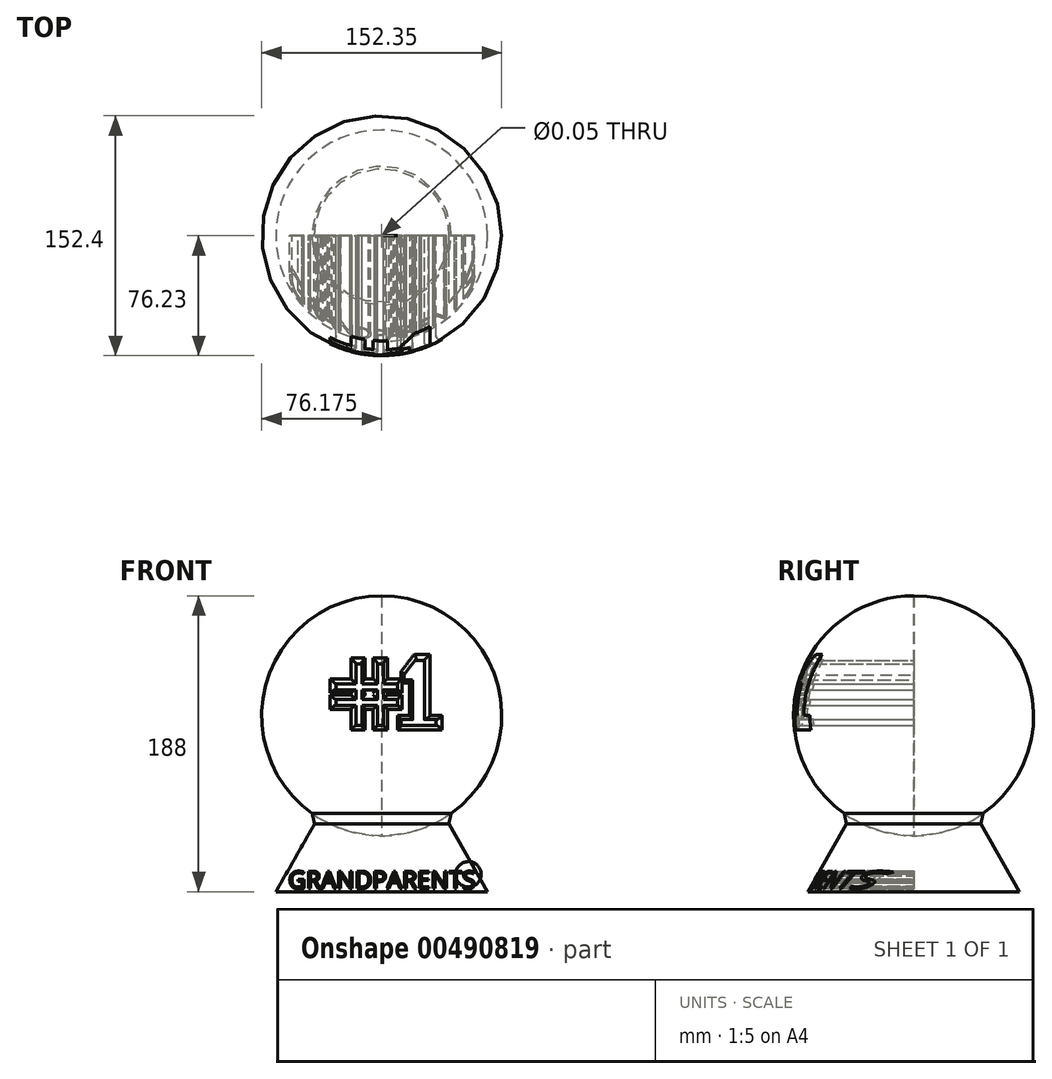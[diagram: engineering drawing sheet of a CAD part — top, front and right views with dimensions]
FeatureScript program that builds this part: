
annotation { "Feature Type Name" : "Feature", "Feature Type Description" : "" }
export const myFeature = defineFeature(function(context is Context, id is Id, definition is map)
    precondition{}
    {
        {
            var Q0;
            Q0=qCreatedBy(makeId("Front.planeOp"),FACE);
            var sketch = newSketch(context, id + "F0", { "sketchPlane" : qUnion([Q0])});
            skArc(sketch, "E0", {"start": v(0, 188) * mm, "mid": v(-76.2, 111.8) * mm, "end": v(0, 35.6) * mm});
            skLineSegment(sketch, "E1", {"start": v(0, 188) * mm, "end": v(0, 35.6) * mm});
            skLineSegment(sketch, "E2", {"start": v(0.03, 35.7) * mm, "end": v(0.03, 188.05) * mm, "construction": true});
            skSolve(sketch);
        }
        {
            var Q0;
            Q0 = qSketchRegion(id + "F0", true);
            var Q1;
            Q1=sQuery(id+"F0.wireOp",EDGE,"E2");
            revolve(context, id + "F1", {"entities" : qUnion([Q0]), "axis" : qUnion([Q1]), "revolveType" : RevolveType.FULL});
        }
        {
            var Q0;
            Q0=qCreatedBy(makeId("Front.planeOp"),FACE);
            var sketch = newSketch(context, id + "F2", { "sketchPlane" : qUnion([Q0])});
            skLineSegment(sketch, "E3", {"start": v(-40.05, 47.52) * mm, "end": v(-67.16, 0) * mm});
            skLineSegment(sketch, "E4", {"start": v(0, 0) * mm, "end": v(0, 64.85) * mm, "construction": true});
            skCircle(sketch, "E5", {"center": v(0, 112.35) * mm, "radius": 76.2 * mm, "construction": true});
            skArc(sketch, "E6", {"start": v(-40.05, 47.52) * mm, "mid": v(-20.9, 38.78) * mm, "end": v(0, 36.15) * mm});
            skLineSegment(sketch, "E7", {"start": v(-67.16, 0) * mm, "end": v(0, 0) * mm});
            skLineSegment(sketch, "E8", {"start": v(0, 0) * mm, "end": v(0, 36.15) * mm});
            skSolve(sketch);
        }
        {
            var Q0;
            Q0=makeQuery(id+"F2.imprint","IMPRINT",FACE,{"disambiguationData":[TD([[makeQuery(id+"F2.imprint","IMPRINT",EDGE,{"derivedFrom":sQuery(id+"F2.wireOp",EDGE,"E3")}),1.0]])]});
            var Q1;
            Q1=sQuery(id+"F2.wireOp",EDGE,"E4");
            revolve(context, id + "F3", {"operationType" : NewBodyOperationType.ADD, "entities" : qUnion([Q0]), "axis" : qUnion([Q1]), "revolveType" : RevolveType.FULL});
        }
        {
            var Q0;
            Q0=makeQuery(id+"F3.boolean.opBoolean","INTERSECT",EDGE,{"derivedFrom":[makeQuery(id+"F1.opRevolve","SWEPT_FACE",FACE,{"disambiguationData":[OSD([sQuery(id+"F0.wireOp",EDGE,"E0")])]}),makeQuery(id+"F3.opRevolve","SWEPT_FACE",FACE,{"disambiguationData":[OSD([sQuery(id+"F2.wireOp",EDGE,"E3")])]})]});
            chamfer(context, id + "F4", {"entities" : qUnion([Q0]), "width" : 5.08 * mm, "tangentPropagation" : true});
        }
        {
            var Q0;
            Q0=qCreatedBy(makeId("Front.planeOp"),FACE);
            var sketch = newSketch(context, id + "F5", { "sketchPlane" : qUnion([Q0])});
            skLineSegment(sketch, "E9", {"start": v(-16.4, 105.63) * mm, "end": v(-16.4, 128.2) * mm});
            skLineSegment(sketch, "E10", {"start": v(-2.72, 105.63) * mm, "end": v(-2.72, 128.2) * mm});
            skLineSegment(sketch, "E11", {"start": v(-29.1, 132) * mm, "end": v(9.98, 132) * mm});
            skLineSegment(sketch, "E12", {"start": v(-29.1, 118.33) * mm, "end": v(9.98, 118.33) * mm});
            skLineSegment(sketch, "E13", {"start": v(-29.1, 132) * mm, "end": v(-29.1, 128.2) * mm});
            skLineSegment(sketch, "E14", {"start": v(-29.1, 128.2) * mm, "end": v(9.98, 128.2) * mm});
            skLineSegment(sketch, "E15", {"start": v(9.98, 128.2) * mm, "end": v(9.98, 132) * mm});
            skLineSegment(sketch, "E16.trimOffspring", {"start": v(-16.4, 132) * mm, "end": v(-16.4, 144.7) * mm});
            skLineSegment(sketch, "E17.trimOffspring", {"start": v(-2.72, 132) * mm, "end": v(-2.72, 144.7) * mm});
            skLineSegment(sketch, "E18", {"start": v(-29.1, 118.33) * mm, "end": v(-29.1, 122.14) * mm});
            skLineSegment(sketch, "E19", {"start": v(-29.1, 122.14) * mm, "end": v(9.98, 122.14) * mm});
            skLineSegment(sketch, "E20", {"start": v(9.98, 118.33) * mm, "end": v(9.98, 122.14) * mm});
            skLineSegment(sketch, "E21", {"start": v(-16.4, 105.63) * mm, "end": v(-12.58, 105.63) * mm});
            skLineSegment(sketch, "E22", {"start": v(-12.58, 105.63) * mm, "end": v(-12.58, 144.7) * mm});
            skLineSegment(sketch, "E23", {"start": v(-16.4, 144.7) * mm, "end": v(-12.58, 144.7) * mm});
            skLineSegment(sketch, "E24", {"start": v(-2.72, 105.63) * mm, "end": v(1.1, 105.63) * mm});
            skLineSegment(sketch, "E25", {"start": v(1.1, 105.63) * mm, "end": v(1.1, 144.7) * mm});
            skLineSegment(sketch, "E26", {"start": v(1.1, 144.7) * mm, "end": v(-2.72, 144.7) * mm});
            skLineSegment(sketch, "E27", {"start": v(12.35, 105.7) * mm, "end": v(34.53, 105.7) * mm});
            skLineSegment(sketch, "E28", {"start": v(34.53, 105.7) * mm, "end": v(34.53, 109.31) * mm});
            skLineSegment(sketch, "E29", {"start": v(34.53, 109.31) * mm, "end": v(27.13, 109.31) * mm});
            skLineSegment(sketch, "E30", {"start": v(27.13, 109.31) * mm, "end": v(27.13, 147.04) * mm});
            skLineSegment(sketch, "E31", {"start": v(27.13, 147.04) * mm, "end": v(21.36, 147.04) * mm});
            skLineSegment(sketch, "E32", {"start": v(21.36, 147.04) * mm, "end": v(14.32, 137.86) * mm});
            skLineSegment(sketch, "E33", {"start": v(14.32, 137.86) * mm, "end": v(14.32, 134.55) * mm});
            skLineSegment(sketch, "E34", {"start": v(14.32, 134.55) * mm, "end": v(19.75, 134.55) * mm});
            skLineSegment(sketch, "E35", {"start": v(12.35, 105.7) * mm, "end": v(12.35, 109.31) * mm});
            skLineSegment(sketch, "E36", {"start": v(12.35, 109.31) * mm, "end": v(19.75, 109.31) * mm});
            skLineSegment(sketch, "E37", {"start": v(19.75, 109.31) * mm, "end": v(19.75, 134.55) * mm});
            skSolve(sketch);
        }
        {
            var Q0;
            Q0 = qSketchRegion(id + "F5", true);
            extrude(context, id + "F6", {"entities" : qUnion([Q0]), "operationType" : NewBodyOperationType.REMOVE, "depth" : 78.74 * mm});
        }
        {
            var Q0;
            Q0=makeQuery(id+"F6.boolean.opBoolean","INTERSECT",EDGE,{"derivedFrom":[makeQuery(id+"F1.opRevolve","SWEPT_FACE",FACE,{"disambiguationData":[OSD([sQuery(id+"F0.wireOp",EDGE,"E0")])]}),makeQuery(id+"F6.opExtrude","SWEPT_FACE",FACE,{"disambiguationData":[OSD([sQuery(id+"F5.wireOp",EDGE,"E30")])]})]});
            var Q1;
            Q1=makeQuery(id+"F6.boolean.opBoolean","INTERSECT",EDGE,{"derivedFrom":[makeQuery(id+"F1.opRevolve","SWEPT_FACE",FACE,{"disambiguationData":[OSD([sQuery(id+"F0.wireOp",EDGE,"E0")])]}),makeQuery(id+"F6.opExtrude","SWEPT_FACE",FACE,{"disambiguationData":[OSD([sQuery(id+"F5.wireOp",EDGE,"E29")])]})]});
            var Q2;
            Q2=makeQuery(id+"F6.boolean.opBoolean","INTERSECT",EDGE,{"derivedFrom":[makeQuery(id+"F1.opRevolve","SWEPT_FACE",FACE,{"disambiguationData":[OSD([sQuery(id+"F0.wireOp",EDGE,"E0")])]}),makeQuery(id+"F6.opExtrude","SWEPT_FACE",FACE,{"disambiguationData":[OSD([sQuery(id+"F5.wireOp",EDGE,"E28")])]})]});
            var Q3;
            Q3=makeQuery(id+"F6.boolean.opBoolean","INTERSECT",EDGE,{"derivedFrom":[makeQuery(id+"F1.opRevolve","SWEPT_FACE",FACE,{"disambiguationData":[OSD([sQuery(id+"F0.wireOp",EDGE,"E0")])]}),makeQuery(id+"F6.opExtrude","SWEPT_FACE",FACE,{"disambiguationData":[OSD([sQuery(id+"F5.wireOp",EDGE,"E27")])]})]});
            var Q4;
            Q4=makeQuery(id+"F6.boolean.opBoolean","INTERSECT",EDGE,{"derivedFrom":[makeQuery(id+"F1.opRevolve","SWEPT_FACE",FACE,{"disambiguationData":[OSD([sQuery(id+"F0.wireOp",EDGE,"E0")])]}),makeQuery(id+"F6.opExtrude","SWEPT_FACE",FACE,{"disambiguationData":[OSD([sQuery(id+"F5.wireOp",EDGE,"E35")])]})]});
            var Q5;
            Q5=makeQuery(id+"F6.boolean.opBoolean","INTERSECT",EDGE,{"derivedFrom":[makeQuery(id+"F1.opRevolve","SWEPT_FACE",FACE,{"disambiguationData":[OSD([sQuery(id+"F0.wireOp",EDGE,"E0")])]}),makeQuery(id+"F6.opExtrude","SWEPT_FACE",FACE,{"disambiguationData":[OSD([sQuery(id+"F5.wireOp",EDGE,"E36")])]})]});
            var Q6;
            Q6=makeQuery(id+"F6.boolean.opBoolean","INTERSECT",EDGE,{"derivedFrom":[makeQuery(id+"F1.opRevolve","SWEPT_FACE",FACE,{"disambiguationData":[OSD([sQuery(id+"F0.wireOp",EDGE,"E0")])]}),makeQuery(id+"F6.opExtrude","SWEPT_FACE",FACE,{"disambiguationData":[OSD([sQuery(id+"F5.wireOp",EDGE,"E37")])]})]});
            var Q7;
            Q7=makeQuery(id+"F6.boolean.opBoolean","INTERSECT",EDGE,{"derivedFrom":[makeQuery(id+"F1.opRevolve","SWEPT_FACE",FACE,{"disambiguationData":[OSD([sQuery(id+"F0.wireOp",EDGE,"E0")])]}),makeQuery(id+"F6.opExtrude","SWEPT_FACE",FACE,{"disambiguationData":[OSD([sQuery(id+"F5.wireOp",EDGE,"E34")])]})]});
            var Q8;
            Q8=makeQuery(id+"F6.boolean.opBoolean","INTERSECT",EDGE,{"derivedFrom":[makeQuery(id+"F1.opRevolve","SWEPT_FACE",FACE,{"disambiguationData":[OSD([sQuery(id+"F0.wireOp",EDGE,"E0")])]}),makeQuery(id+"F6.opExtrude","SWEPT_FACE",FACE,{"disambiguationData":[OSD([sQuery(id+"F5.wireOp",EDGE,"E33")])]})]});
            var Q9;
            Q9=makeQuery(id+"F6.boolean.opBoolean","INTERSECT",EDGE,{"derivedFrom":[makeQuery(id+"F1.opRevolve","SWEPT_FACE",FACE,{"disambiguationData":[OSD([sQuery(id+"F0.wireOp",EDGE,"E0")])]}),makeQuery(id+"F6.opExtrude","SWEPT_FACE",FACE,{"disambiguationData":[OSD([sQuery(id+"F5.wireOp",EDGE,"E32")])]})]});
            var Q10;
            Q10=makeQuery(id+"F6.boolean.opBoolean","INTERSECT",EDGE,{"derivedFrom":[makeQuery(id+"F1.opRevolve","SWEPT_FACE",FACE,{"disambiguationData":[OSD([sQuery(id+"F0.wireOp",EDGE,"E0")])]}),makeQuery(id+"F6.opExtrude","SWEPT_FACE",FACE,{"disambiguationData":[OSD([sQuery(id+"F5.wireOp",EDGE,"E31")])]})]});
            fillet(context, id + "F7", {"entities" : qUnion([Q0, Q1, Q2, Q3, Q4, Q5, Q6, Q7, Q8, Q9, Q10]), "radius" : 2.54 * mm, "tangentPropagation" : true, "allowEdgeOverflow" : false});
        }
        {
            var Q0;
            Q0=qCreatedBy(makeId("Front.planeOp"),FACE);
            var sketch = newSketch(context, id + "F8", { "sketchPlane" : qUnion([Q0])});
            skText(sketch, "E38", { "text": "GRANDPARENTS", "fontName": "OpenSans-Regular.ttf"});
            const initialGuessF8  = {"E38": [-0.05927, 0.002, 1, 0, 0.01108]};
            skSetInitialGuess(sketch, initialGuessF8);
            skSolve(sketch);
        }
        {
            var Q0;
            Q0 = qSketchRegion(id + "F8", true);
            extrude(context, id + "F9", {"entities" : qUnion([Q0]), "operationType" : NewBodyOperationType.REMOVE, "depth" : 66.04 * mm});
        }
        {
            var Q0;
            {var subQ0=sQuery(id+"F5.wireOp",EDGE,"E14");var subQ1=sQuery(id+"F5.wireOp",EDGE,"E10");var subQ2=makeQuery(id+"F5.imprint","INTERSECT",VERTEX,{"derivedFrom":[subQ1,subQ0]});Q0=makeQuery(id+"F6.boolean.opBoolean","SPLIT",FACE,{"disambiguationData":[TD([makeQuery(id+"F6.opExtrude","SWEPT_FACE",FACE,{"disambiguationData":[OSD([subQ1]),TDD([makeQuery(id+"F5.imprint","IMPRINT",EDGE,{"disambiguationData":[TD([[subQ2,1.0]])],"derivedFrom":subQ1})])]})])],"derivedFrom":makeQuery(id+"F1.opRevolve","SWEPT_FACE",FACE,{"disambiguationData":[OSD([sQuery(id+"F0.wireOp",EDGE,"E0")])]})});}
            var Q1;
            {var subQ0=sQuery(id+"F5.wireOp",EDGE,"E11");Q1=makeQuery(id+"F6.boolean.opBoolean","INTERSECT",EDGE,{"derivedFrom":[makeQuery(id+"F1.opRevolve","SWEPT_FACE",FACE,{"disambiguationData":[OSD([sQuery(id+"F0.wireOp",EDGE,"E0")])]}),makeQuery(id+"F6.opExtrude","SWEPT_FACE",FACE,{"disambiguationData":[OSD([subQ0]),TDD([makeQuery(id+"F5.imprint","IMPRINT",EDGE,{"disambiguationData":[TD([[makeQuery(id+"F5.imprint","INTERSECT",VERTEX,{"derivedFrom":[subQ0,sQuery(id+"F5.wireOp",EDGE,"E17.trimOffspring")]}),1.0]])],"derivedFrom":subQ0})])]})]});}
            var Q2;
            {var subQ0=sQuery(id+"F5.wireOp",EDGE,"E22");Q2=makeQuery(id+"F6.boolean.opBoolean","INTERSECT",EDGE,{"derivedFrom":[makeQuery(id+"F1.opRevolve","SWEPT_FACE",FACE,{"disambiguationData":[OSD([sQuery(id+"F0.wireOp",EDGE,"E0")])]}),makeQuery(id+"F6.opExtrude","SWEPT_FACE",FACE,{"disambiguationData":[OSD([subQ0]),TDD([makeQuery(id+"F5.imprint","IMPRINT",EDGE,{"disambiguationData":[TD([[makeQuery(id+"F5.imprint","INTERSECT",VERTEX,{"derivedFrom":[subQ0,sQuery(id+"F5.wireOp",EDGE,"E23")]}),1.0]])],"derivedFrom":subQ0})])]})]});}
            var Q3;
            Q3=makeQuery(id+"F6.boolean.opBoolean","INTERSECT",EDGE,{"derivedFrom":[makeQuery(id+"F1.opRevolve","SWEPT_FACE",FACE,{"disambiguationData":[OSD([sQuery(id+"F0.wireOp",EDGE,"E0")])]}),makeQuery(id+"F6.opExtrude","SWEPT_FACE",FACE,{"disambiguationData":[OSD([sQuery(id+"F5.wireOp",EDGE,"E23")])]})]});
            var Q4;
            Q4=makeQuery(id+"F6.boolean.opBoolean","INTERSECT",EDGE,{"derivedFrom":[makeQuery(id+"F1.opRevolve","SWEPT_FACE",FACE,{"disambiguationData":[OSD([sQuery(id+"F0.wireOp",EDGE,"E0")])]}),makeQuery(id+"F6.opExtrude","SWEPT_FACE",FACE,{"disambiguationData":[OSD([sQuery(id+"F5.wireOp",EDGE,"E16.trimOffspring")])]})]});
            var Q5;
            {var subQ0=sQuery(id+"F5.wireOp",EDGE,"E11");Q5=makeQuery(id+"F6.boolean.opBoolean","INTERSECT",EDGE,{"derivedFrom":[makeQuery(id+"F1.opRevolve","SWEPT_FACE",FACE,{"disambiguationData":[OSD([sQuery(id+"F0.wireOp",EDGE,"E0")])]}),makeQuery(id+"F6.opExtrude","SWEPT_FACE",FACE,{"disambiguationData":[OSD([subQ0]),TDD([makeQuery(id+"F5.imprint","IMPRINT",EDGE,{"disambiguationData":[TD([[makeQuery(id+"F5.imprint","INTERSECT",VERTEX,{"derivedFrom":[subQ0,sQuery(id+"F5.wireOp",EDGE,"E13")]}),-1.0]])],"derivedFrom":subQ0})])]})]});}
            var Q6;
            Q6=makeQuery(id+"F6.boolean.opBoolean","INTERSECT",EDGE,{"derivedFrom":[makeQuery(id+"F1.opRevolve","SWEPT_FACE",FACE,{"disambiguationData":[OSD([sQuery(id+"F0.wireOp",EDGE,"E0")])]}),makeQuery(id+"F6.opExtrude","SWEPT_FACE",FACE,{"disambiguationData":[OSD([sQuery(id+"F5.wireOp",EDGE,"E13")])]})]});
            var Q7;
            {var subQ0=sQuery(id+"F5.wireOp",EDGE,"E14");Q7=makeQuery(id+"F6.boolean.opBoolean","INTERSECT",EDGE,{"derivedFrom":[makeQuery(id+"F1.opRevolve","SWEPT_FACE",FACE,{"disambiguationData":[OSD([sQuery(id+"F0.wireOp",EDGE,"E0")])]}),makeQuery(id+"F6.opExtrude","SWEPT_FACE",FACE,{"disambiguationData":[OSD([subQ0]),TDD([makeQuery(id+"F5.imprint","IMPRINT",EDGE,{"disambiguationData":[TD([[makeQuery(id+"F5.imprint","INTERSECT",VERTEX,{"derivedFrom":[sQuery(id+"F5.wireOp",EDGE,"E9"),subQ0]}),1.0]])],"derivedFrom":subQ0})])]})]});}
            var Q8;
            {var subQ0=sQuery(id+"F5.wireOp",EDGE,"E9");Q8=makeQuery(id+"F6.boolean.opBoolean","INTERSECT",EDGE,{"derivedFrom":[makeQuery(id+"F1.opRevolve","SWEPT_FACE",FACE,{"disambiguationData":[OSD([sQuery(id+"F0.wireOp",EDGE,"E0")])]}),makeQuery(id+"F6.opExtrude","SWEPT_FACE",FACE,{"disambiguationData":[OSD([subQ0]),TDD([makeQuery(id+"F5.imprint","IMPRINT",EDGE,{"disambiguationData":[TD([[makeQuery(id+"F5.imprint","INTERSECT",VERTEX,{"derivedFrom":[subQ0,sQuery(id+"F5.wireOp",EDGE,"E14")]}),1.0]])],"derivedFrom":subQ0})])]})]});}
            var Q9;
            {var subQ0=sQuery(id+"F5.wireOp",EDGE,"E19");Q9=makeQuery(id+"F6.boolean.opBoolean","INTERSECT",EDGE,{"derivedFrom":[makeQuery(id+"F1.opRevolve","SWEPT_FACE",FACE,{"disambiguationData":[OSD([sQuery(id+"F0.wireOp",EDGE,"E0")])]}),makeQuery(id+"F6.opExtrude","SWEPT_FACE",FACE,{"disambiguationData":[OSD([subQ0]),TDD([makeQuery(id+"F5.imprint","IMPRINT",EDGE,{"disambiguationData":[TD([[makeQuery(id+"F5.imprint","INTERSECT",VERTEX,{"derivedFrom":[sQuery(id+"F5.wireOp",EDGE,"E18"),subQ0]}),-1.0]])],"derivedFrom":subQ0})])]})]});}
            var Q10;
            Q10=makeQuery(id+"F6.boolean.opBoolean","INTERSECT",EDGE,{"derivedFrom":[makeQuery(id+"F1.opRevolve","SWEPT_FACE",FACE,{"disambiguationData":[OSD([sQuery(id+"F0.wireOp",EDGE,"E0")])]}),makeQuery(id+"F6.opExtrude","SWEPT_FACE",FACE,{"disambiguationData":[OSD([sQuery(id+"F5.wireOp",EDGE,"E18")])]})]});
            var Q11;
            {var subQ0=sQuery(id+"F5.wireOp",EDGE,"E12");Q11=makeQuery(id+"F6.boolean.opBoolean","INTERSECT",EDGE,{"derivedFrom":[makeQuery(id+"F1.opRevolve","SWEPT_FACE",FACE,{"disambiguationData":[OSD([sQuery(id+"F0.wireOp",EDGE,"E0")])]}),makeQuery(id+"F6.opExtrude","SWEPT_FACE",FACE,{"disambiguationData":[OSD([subQ0]),TDD([makeQuery(id+"F5.imprint","IMPRINT",EDGE,{"disambiguationData":[TD([[makeQuery(id+"F5.imprint","INTERSECT",VERTEX,{"derivedFrom":[subQ0,sQuery(id+"F5.wireOp",EDGE,"E18")]}),-1.0]])],"derivedFrom":subQ0})])]})]});}
            var Q12;
            {var subQ0=sQuery(id+"F5.wireOp",EDGE,"E9");Q12=makeQuery(id+"F6.boolean.opBoolean","INTERSECT",EDGE,{"derivedFrom":[makeQuery(id+"F1.opRevolve","SWEPT_FACE",FACE,{"disambiguationData":[OSD([sQuery(id+"F0.wireOp",EDGE,"E0")])]}),makeQuery(id+"F6.opExtrude","SWEPT_FACE",FACE,{"disambiguationData":[OSD([subQ0]),TDD([makeQuery(id+"F5.imprint","IMPRINT",EDGE,{"disambiguationData":[TD([[makeQuery(id+"F5.imprint","INTERSECT",VERTEX,{"derivedFrom":[subQ0,sQuery(id+"F5.wireOp",EDGE,"E21")]}),-1.0]])],"derivedFrom":subQ0})])]})]});}
            var Q13;
            Q13=makeQuery(id+"F6.boolean.opBoolean","INTERSECT",EDGE,{"derivedFrom":[makeQuery(id+"F1.opRevolve","SWEPT_FACE",FACE,{"disambiguationData":[OSD([sQuery(id+"F0.wireOp",EDGE,"E0")])]}),makeQuery(id+"F6.opExtrude","SWEPT_FACE",FACE,{"disambiguationData":[OSD([sQuery(id+"F5.wireOp",EDGE,"E21")])]})]});
            var Q14;
            {var subQ0=sQuery(id+"F5.wireOp",EDGE,"E22");Q14=makeQuery(id+"F6.boolean.opBoolean","INTERSECT",EDGE,{"derivedFrom":[makeQuery(id+"F1.opRevolve","SWEPT_FACE",FACE,{"disambiguationData":[OSD([sQuery(id+"F0.wireOp",EDGE,"E0")])]}),makeQuery(id+"F6.opExtrude","SWEPT_FACE",FACE,{"disambiguationData":[OSD([subQ0]),TDD([makeQuery(id+"F5.imprint","IMPRINT",EDGE,{"disambiguationData":[TD([[makeQuery(id+"F5.imprint","INTERSECT",VERTEX,{"derivedFrom":[sQuery(id+"F5.wireOp",EDGE,"E21"),subQ0]}),-1.0]])],"derivedFrom":subQ0})])]})]});}
            var Q15;
            {var subQ0=sQuery(id+"F5.wireOp",EDGE,"E12");Q15=makeQuery(id+"F6.boolean.opBoolean","INTERSECT",EDGE,{"derivedFrom":[makeQuery(id+"F1.opRevolve","SWEPT_FACE",FACE,{"disambiguationData":[OSD([sQuery(id+"F0.wireOp",EDGE,"E0")])]}),makeQuery(id+"F6.opExtrude","SWEPT_FACE",FACE,{"disambiguationData":[OSD([subQ0]),TDD([makeQuery(id+"F5.imprint","IMPRINT",EDGE,{"disambiguationData":[TD([[makeQuery(id+"F5.imprint","INTERSECT",VERTEX,{"derivedFrom":[sQuery(id+"F5.wireOp",EDGE,"E10"),subQ0]}),1.0]])],"derivedFrom":subQ0})])]})]});}
            var Q16;
            {var subQ0=sQuery(id+"F5.wireOp",EDGE,"E10");Q16=makeQuery(id+"F6.boolean.opBoolean","INTERSECT",EDGE,{"derivedFrom":[makeQuery(id+"F1.opRevolve","SWEPT_FACE",FACE,{"disambiguationData":[OSD([sQuery(id+"F0.wireOp",EDGE,"E0")])]}),makeQuery(id+"F6.opExtrude","SWEPT_FACE",FACE,{"disambiguationData":[OSD([subQ0]),TDD([makeQuery(id+"F5.imprint","IMPRINT",EDGE,{"disambiguationData":[TD([[makeQuery(id+"F5.imprint","INTERSECT",VERTEX,{"derivedFrom":[subQ0,sQuery(id+"F5.wireOp",EDGE,"E24")]}),-1.0]])],"derivedFrom":subQ0})])]})]});}
            var Q17;
            Q17=makeQuery(id+"F6.boolean.opBoolean","INTERSECT",EDGE,{"derivedFrom":[makeQuery(id+"F1.opRevolve","SWEPT_FACE",FACE,{"disambiguationData":[OSD([sQuery(id+"F0.wireOp",EDGE,"E0")])]}),makeQuery(id+"F6.opExtrude","SWEPT_FACE",FACE,{"disambiguationData":[OSD([sQuery(id+"F5.wireOp",EDGE,"E24")])]})]});
            var Q18;
            {var subQ0=sQuery(id+"F5.wireOp",EDGE,"E25");Q18=makeQuery(id+"F6.boolean.opBoolean","INTERSECT",EDGE,{"derivedFrom":[makeQuery(id+"F1.opRevolve","SWEPT_FACE",FACE,{"disambiguationData":[OSD([sQuery(id+"F0.wireOp",EDGE,"E0")])]}),makeQuery(id+"F6.opExtrude","SWEPT_FACE",FACE,{"disambiguationData":[OSD([subQ0]),TDD([makeQuery(id+"F5.imprint","IMPRINT",EDGE,{"disambiguationData":[TD([[makeQuery(id+"F5.imprint","INTERSECT",VERTEX,{"derivedFrom":[sQuery(id+"F5.wireOp",EDGE,"E24"),subQ0]}),-1.0]])],"derivedFrom":subQ0})])]})]});}
            var Q19;
            {var subQ0=sQuery(id+"F5.wireOp",EDGE,"E12");Q19=makeQuery(id+"F6.boolean.opBoolean","INTERSECT",EDGE,{"derivedFrom":[makeQuery(id+"F1.opRevolve","SWEPT_FACE",FACE,{"disambiguationData":[OSD([sQuery(id+"F0.wireOp",EDGE,"E0")])]}),makeQuery(id+"F6.opExtrude","SWEPT_FACE",FACE,{"disambiguationData":[OSD([subQ0]),TDD([makeQuery(id+"F5.imprint","IMPRINT",EDGE,{"disambiguationData":[TD([[makeQuery(id+"F5.imprint","INTERSECT",VERTEX,{"derivedFrom":[subQ0,sQuery(id+"F5.wireOp",EDGE,"E20")]}),1.0]])],"derivedFrom":subQ0})])]})]});}
            var Q20;
            Q20=makeQuery(id+"F6.boolean.opBoolean","INTERSECT",EDGE,{"derivedFrom":[makeQuery(id+"F1.opRevolve","SWEPT_FACE",FACE,{"disambiguationData":[OSD([sQuery(id+"F0.wireOp",EDGE,"E0")])]}),makeQuery(id+"F6.opExtrude","SWEPT_FACE",FACE,{"disambiguationData":[OSD([sQuery(id+"F5.wireOp",EDGE,"E20")])]})]});
            var Q21;
            {var subQ0=sQuery(id+"F5.wireOp",EDGE,"E19");Q21=makeQuery(id+"F6.boolean.opBoolean","INTERSECT",EDGE,{"derivedFrom":[makeQuery(id+"F1.opRevolve","SWEPT_FACE",FACE,{"disambiguationData":[OSD([sQuery(id+"F0.wireOp",EDGE,"E0")])]}),makeQuery(id+"F6.opExtrude","SWEPT_FACE",FACE,{"disambiguationData":[OSD([subQ0]),TDD([makeQuery(id+"F5.imprint","IMPRINT",EDGE,{"disambiguationData":[TD([[makeQuery(id+"F5.imprint","INTERSECT",VERTEX,{"derivedFrom":[subQ0,sQuery(id+"F5.wireOp",EDGE,"E20")]}),1.0]])],"derivedFrom":subQ0})])]})]});}
            var Q22;
            {var subQ0=sQuery(id+"F5.wireOp",EDGE,"E25");Q22=makeQuery(id+"F6.boolean.opBoolean","INTERSECT",EDGE,{"derivedFrom":[makeQuery(id+"F1.opRevolve","SWEPT_FACE",FACE,{"disambiguationData":[OSD([sQuery(id+"F0.wireOp",EDGE,"E0")])]}),makeQuery(id+"F6.opExtrude","SWEPT_FACE",FACE,{"disambiguationData":[OSD([subQ0]),TDD([makeQuery(id+"F5.imprint","IMPRINT",EDGE,{"disambiguationData":[TD([[makeQuery(id+"F5.imprint","INTERSECT",VERTEX,{"derivedFrom":[sQuery(id+"F5.wireOp",EDGE,"E14"),subQ0]}),1.0]])],"derivedFrom":subQ0})])]})]});}
            var Q23;
            Q23=makeQuery(id+"F6.boolean.opBoolean","INTERSECT",EDGE,{"derivedFrom":[makeQuery(id+"F1.opRevolve","SWEPT_FACE",FACE,{"disambiguationData":[OSD([sQuery(id+"F0.wireOp",EDGE,"E0")])]}),makeQuery(id+"F6.opExtrude","SWEPT_FACE",FACE,{"disambiguationData":[OSD([sQuery(id+"F5.wireOp",EDGE,"E15")])]})]});
            var Q24;
            {var subQ0=sQuery(id+"F5.wireOp",EDGE,"E11");Q24=makeQuery(id+"F6.boolean.opBoolean","INTERSECT",EDGE,{"derivedFrom":[makeQuery(id+"F1.opRevolve","SWEPT_FACE",FACE,{"disambiguationData":[OSD([sQuery(id+"F0.wireOp",EDGE,"E0")])]}),makeQuery(id+"F6.opExtrude","SWEPT_FACE",FACE,{"disambiguationData":[OSD([subQ0]),TDD([makeQuery(id+"F5.imprint","IMPRINT",EDGE,{"disambiguationData":[TD([[makeQuery(id+"F5.imprint","INTERSECT",VERTEX,{"derivedFrom":[subQ0,sQuery(id+"F5.wireOp",EDGE,"E15")]}),1.0]])],"derivedFrom":subQ0})])]})]});}
            var Q25;
            {var subQ0=sQuery(id+"F5.wireOp",EDGE,"E14");Q25=makeQuery(id+"F6.boolean.opBoolean","INTERSECT",EDGE,{"derivedFrom":[makeQuery(id+"F1.opRevolve","SWEPT_FACE",FACE,{"disambiguationData":[OSD([sQuery(id+"F0.wireOp",EDGE,"E0")])]}),makeQuery(id+"F6.opExtrude","SWEPT_FACE",FACE,{"disambiguationData":[OSD([subQ0]),TDD([makeQuery(id+"F5.imprint","IMPRINT",EDGE,{"disambiguationData":[TD([[makeQuery(id+"F5.imprint","INTERSECT",VERTEX,{"derivedFrom":[subQ0,sQuery(id+"F5.wireOp",EDGE,"E15")]}),1.0]])],"derivedFrom":subQ0})])]})]});}
            var Q26;
            {var subQ0=sQuery(id+"F5.wireOp",EDGE,"E25");Q26=makeQuery(id+"F6.boolean.opBoolean","INTERSECT",EDGE,{"derivedFrom":[makeQuery(id+"F1.opRevolve","SWEPT_FACE",FACE,{"disambiguationData":[OSD([sQuery(id+"F0.wireOp",EDGE,"E0")])]}),makeQuery(id+"F6.opExtrude","SWEPT_FACE",FACE,{"disambiguationData":[OSD([subQ0]),TDD([makeQuery(id+"F5.imprint","IMPRINT",EDGE,{"disambiguationData":[TD([[makeQuery(id+"F5.imprint","INTERSECT",VERTEX,{"derivedFrom":[subQ0,sQuery(id+"F5.wireOp",EDGE,"E26")]}),1.0]])],"derivedFrom":subQ0})])]})]});}
            var Q27;
            Q27=makeQuery(id+"F6.boolean.opBoolean","INTERSECT",EDGE,{"derivedFrom":[makeQuery(id+"F1.opRevolve","SWEPT_FACE",FACE,{"disambiguationData":[OSD([sQuery(id+"F0.wireOp",EDGE,"E0")])]}),makeQuery(id+"F6.opExtrude","SWEPT_FACE",FACE,{"disambiguationData":[OSD([sQuery(id+"F5.wireOp",EDGE,"E26")])]})]});
            var Q28;
            Q28=makeQuery(id+"F6.boolean.opBoolean","INTERSECT",EDGE,{"derivedFrom":[makeQuery(id+"F1.opRevolve","SWEPT_FACE",FACE,{"disambiguationData":[OSD([sQuery(id+"F0.wireOp",EDGE,"E0")])]}),makeQuery(id+"F6.opExtrude","SWEPT_FACE",FACE,{"disambiguationData":[OSD([sQuery(id+"F5.wireOp",EDGE,"E17.trimOffspring")])]})]});
            fillet(context, id + "F10", {"entities" : qUnion([Q0, Q1, Q2, Q3, Q4, Q5, Q6, Q7, Q8, Q9, Q10, Q11, Q12, Q13, Q14, Q15, Q16, Q17, Q18, Q19, Q20, Q21, Q22, Q23, Q24, Q25, Q26, Q27, Q28]), "radius" : 2.54 * mm, "tangentPropagation" : true, "allowEdgeOverflow" : false});
        }
    });
